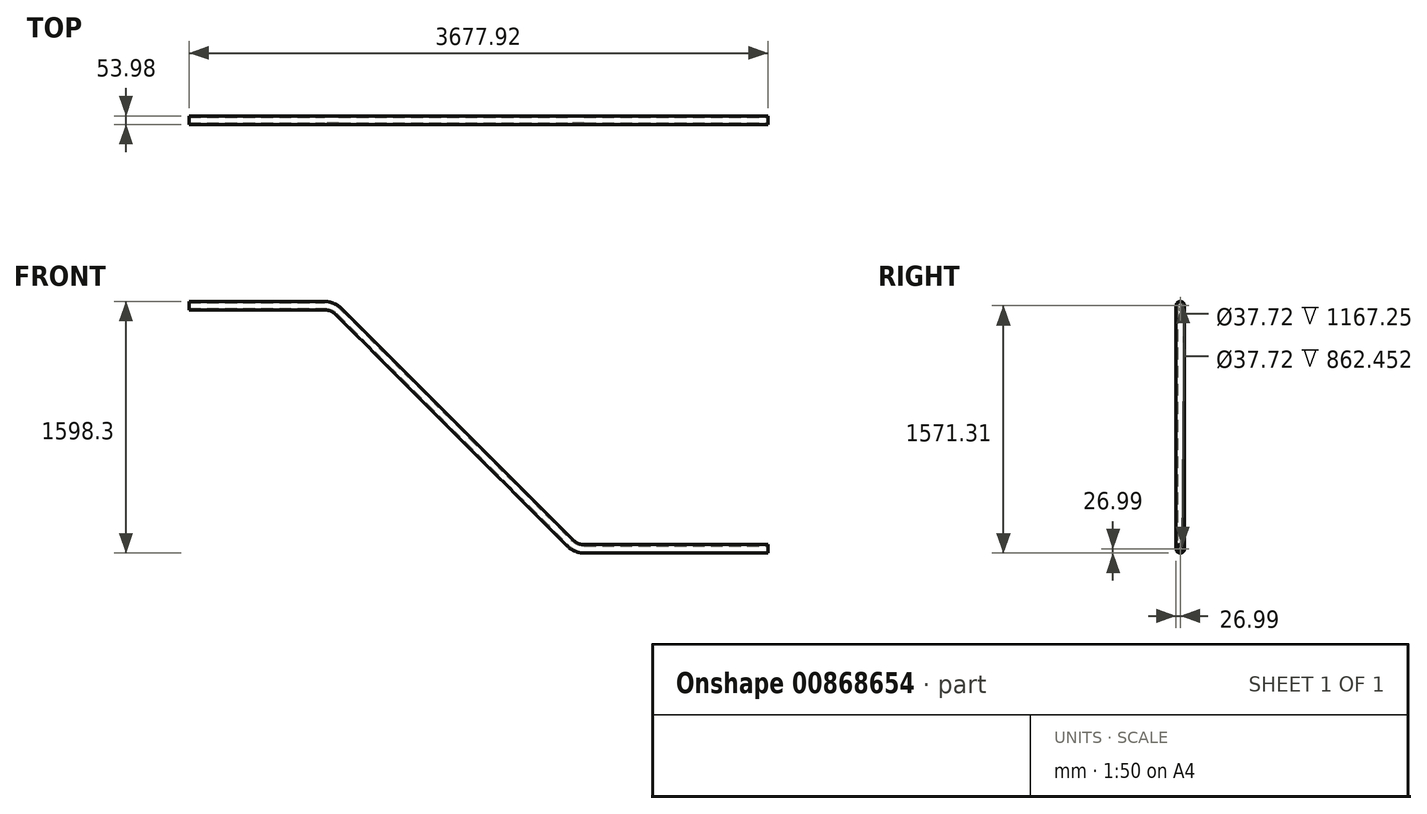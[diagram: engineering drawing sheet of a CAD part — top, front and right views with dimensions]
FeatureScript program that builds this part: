
annotation { "Feature Type Name" : "Feature", "Feature Type Description" : "" }
export const myFeature = defineFeature(function(context is Context, id is Id, definition is map)
    precondition{}
    {
        {
            var Q0;
            Q0=qCreatedBy(makeId("Front.planeOp"),FACE);
            var sketch = newSketch(context, id + "F0", { "sketchPlane" : qUnion([Q0])});
            skLineSegment(sketch, "E0", {"start": v(0, 0) * mm, "end": v(862.45, 0) * mm});
            skLineSegment(sketch, "E1", {"start": v(951.13, -36.73) * mm, "end": v(2421.99, -1507.59) * mm});
            skLineSegment(sketch, "E2", {"start": v(2510.67, -1544.32) * mm, "end": v(3677.92, -1544.32) * mm});
            skLineSegment(sketch, "E3", {"start": v(2458.72, -1544.32) * mm, "end": v(1515.86, -1544.32) * mm, "construction": true});
            skPoint(sketch, "E4.visualSharp", {"position": v(914.4, 0) * mm});
            skArc(sketch, "E4.filletArc", {"start": v(951.13, -36.73) * mm, "mid": v(910.45, -9.55) * mm, "end": v(862.45, 0) * mm});
            skPoint(sketch, "E5.visualSharp", {"position": v(2458.72, -1544.32) * mm});
            skArc(sketch, "E5.filletArc", {"start": v(2421.99, -1507.59) * mm, "mid": v(2462.67, -1534.77) * mm, "end": v(2510.67, -1544.32) * mm});
            skSolve(sketch);
        }
        {
            var Q0;
            Q0=qCreatedBy(makeId("Right.planeOp"),FACE);
            var sketch = newSketch(context, id + "F1", { "sketchPlane" : qUnion([Q0])});
            skCircle(sketch, "E6", {"center": v(0, 0) * mm, "radius": 18.86 * mm});
            skCircle(sketch, "E7", {"center": v(0, 0) * mm, "radius": 26.99 * mm});
            skSolve(sketch);
        }
        {
            var Q0;
            Q0=makeQuery(id+"F1.imprint","IMPRINT",FACE,{"disambiguationData":[TD([[makeQuery(id+"F1.imprint","IMPRINT",EDGE,{"derivedFrom":sQuery(id+"F1.wireOp",EDGE,"E6")}),-1.0]])]});
            var Q1;
            Q1=sQuery(id+"F0.wireOp",EDGE,"E0");
            var Q2;
            Q2=sQuery(id+"F0.wireOp",EDGE,"E4.filletArc");
            var Q3;
            Q3=sQuery(id+"F0.wireOp",EDGE,"E1");
            var Q4;
            Q4=sQuery(id+"F0.wireOp",EDGE,"E5.filletArc");
            var Q5;
            Q5=sQuery(id+"F0.wireOp",EDGE,"E2");
            sweep(context, id + "F2", {"profiles" : qUnion([Q0]), "path" : qUnion([Q1, Q2, Q3, Q4, Q5])});
        }
    });
